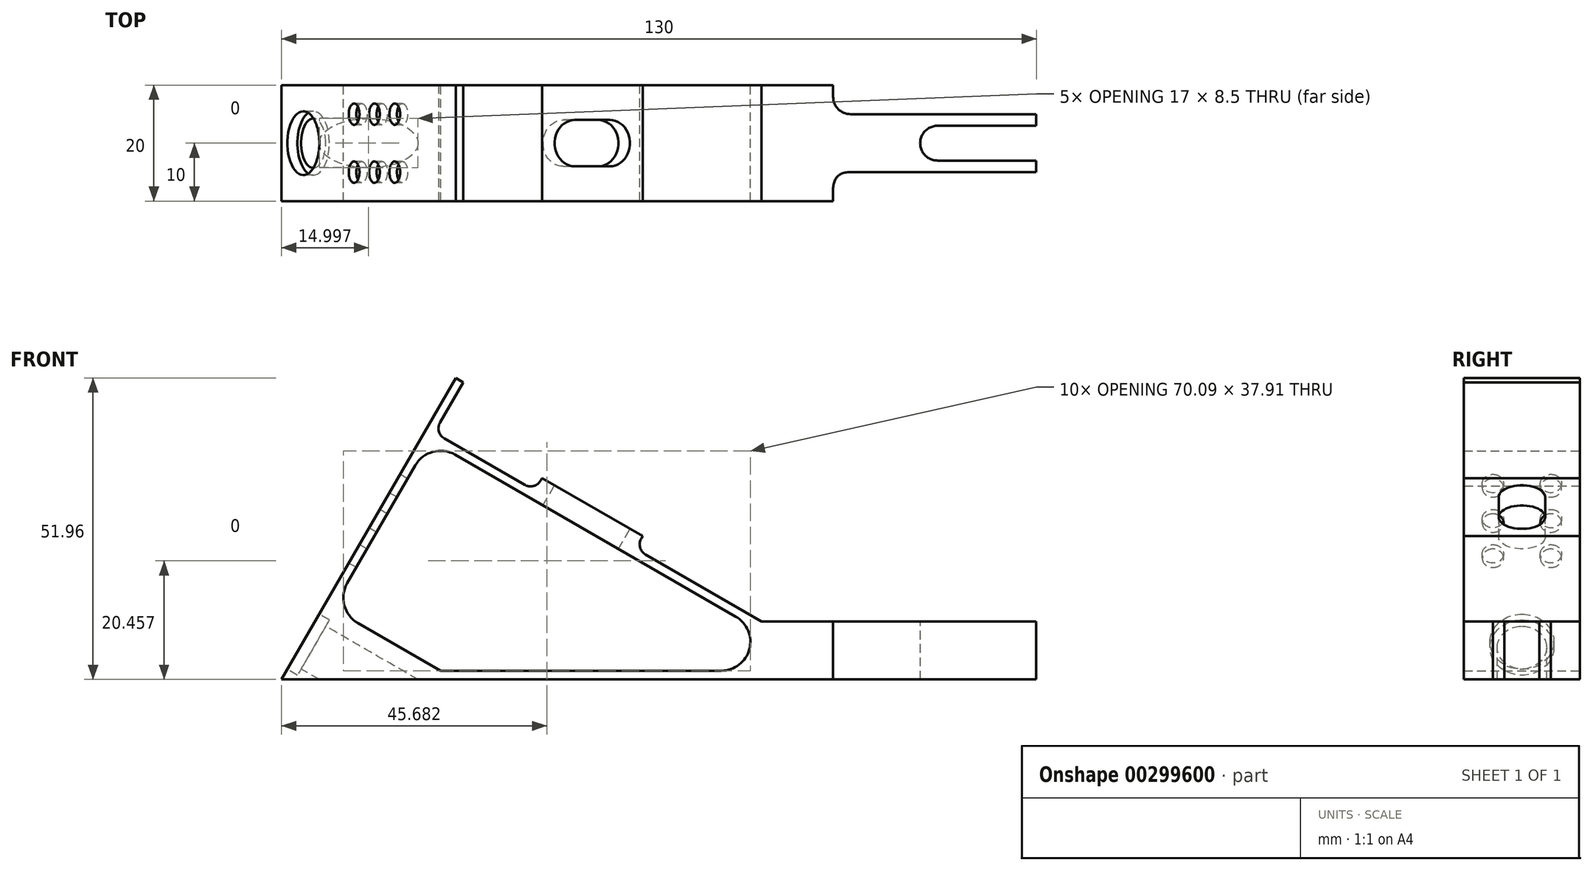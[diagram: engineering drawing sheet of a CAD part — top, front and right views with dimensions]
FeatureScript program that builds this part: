
annotation { "Feature Type Name" : "Feature", "Feature Type Description" : "" }
export const myFeature = defineFeature(function(context is Context, id is Id, definition is map)
    precondition{}
    {
        {
            var Q0;
            Q0=qCreatedBy(makeId("Front.planeOp"),FACE);
            var sketch = newSketch(context, id + "F0", { "sketchPlane" : qUnion([Q0])});
            skLineSegment(sketch, "E0", {"start": v(47.67, 58.9) * mm, "end": v(48.97, 58.14) * mm});
            skLineSegment(sketch, "E1", {"start": v(48.97, 58.14) * mm, "end": v(43.97, 49.48) * mm});
            skLineSegment(sketch, "E2", {"start": v(43.97, 49.48) * mm, "end": v(48.97, 46.6) * mm});
            skLineSegment(sketch, "E3", {"start": v(78.6, 29.48) * mm, "end": v(100.35, 16.93) * mm});
            skLineSegment(sketch, "E4", {"start": v(100.35, 16.93) * mm, "end": v(147.67, 16.93) * mm});
            skLineSegment(sketch, "E5", {"start": v(147.67, 16.93) * mm, "end": v(147.67, 6.93) * mm});
            skLineSegment(sketch, "E6", {"start": v(147.67, 6.93) * mm, "end": v(17.67, 6.93) * mm});
            skLineSegment(sketch, "E7", {"start": v(47.67, 58.9) * mm, "end": v(17.67, 6.93) * mm});
            skLineSegment(sketch, "E8", {"start": v(30.8, 16.67) * mm, "end": v(45.07, 8.43) * mm});
            skLineSegment(sketch, "E9", {"start": v(45.07, 8.43) * mm, "end": v(93.4, 8.43) * mm});
            skArc(sketch, "E10", {"start": v(93.4, 8.43) * mm, "mid": v(98.24, 12.14) * mm, "end": v(95.9, 17.76) * mm});
            skLineSegment(sketch, "E11", {"start": v(95.9, 17.76) * mm, "end": v(47.55, 45.68) * mm});
            skArc(sketch, "E12", {"start": v(47.55, 45.68) * mm, "mid": v(43.75, 46.18) * mm, "end": v(40.72, 43.85) * mm});
            skLineSegment(sketch, "E13", {"start": v(40.72, 43.85) * mm, "end": v(28.97, 23.5) * mm});
            skArc(sketch, "E14", {"start": v(28.97, 23.5) * mm, "mid": v(28.47, 19.7) * mm, "end": v(30.8, 16.67) * mm});
            skPoint(sketch, "E15.start.orphan", {"position": v(50.22, 48.76) * mm});
            skPoint(sketch, "E16.start.orphan", {"position": v(67.54, 38.76) * mm});
            skLineSegment(sketch, "E17", {"start": v(48.97, 46.6) * mm, "end": v(61.29, 39.48) * mm});
            skLineSegment(sketch, "E18", {"start": v(61.29, 39.48) * mm, "end": v(62.54, 41.65) * mm});
            skLineSegment(sketch, "E19", {"start": v(62.54, 41.65) * mm, "end": v(79.86, 31.65) * mm});
            skLineSegment(sketch, "E20", {"start": v(79.86, 31.65) * mm, "end": v(78.6, 29.48) * mm});
            skPoint(sketch, "E21.orphan", {"position": v(66.29, 36.6) * mm});
            skSolve(sketch);
        }
        {
            var Q0;
            Q0 = qSketchRegion(id + "F0", true);
            extrude(context, id + "F1", {"entities" : qUnion([Q0]), "depth" : 20 * mm});
        }
        {
            var Q0;
            Q0=makeQuery(id+"F1.opExtrude","CAP_FACE",FACE,{"disambiguationData":[OSD([sQuery(id+"F0.wireOp",EDGE,"E0"),sQuery(id+"F0.wireOp",EDGE,"E1"),sQuery(id+"F0.wireOp",EDGE,"E2"),sQuery(id+"F0.wireOp",EDGE,"u1qnqnEZ-ZZXt-tcXC-5rbI-ApPhX4VsB7uH"),sQuery(id+"F0.wireOp",EDGE,"E15"),sQuery(id+"F0.wireOp",EDGE,"E16"),sQuery(id+"F0.wireOp",EDGE,"E3"),sQuery(id+"F0.wireOp",EDGE,"E4"),sQuery(id+"F0.wireOp",EDGE,"E5"),sQuery(id+"F0.wireOp",EDGE,"E6"),sQuery(id+"F0.wireOp",EDGE,"E7"),sQuery(id+"F0.wireOp",EDGE,"E8"),sQuery(id+"F0.wireOp",EDGE,"E9"),sQuery(id+"F0.wireOp",EDGE,"E10"),sQuery(id+"F0.wireOp",EDGE,"E11"),sQuery(id+"F0.wireOp",EDGE,"E12"),sQuery(id+"F0.wireOp",EDGE,"E13"),sQuery(id+"F0.wireOp",EDGE,"E14")])],"isStart":false});
            var sketch = newSketch(context, id + "F2", { "sketchPlane" : qUnion([Q0])});
            skLineSegment(sketch, "E22", {"start": v(112.67, 16.93) * mm, "end": v(112.67, 6.93) * mm});
            skSolve(sketch);
        }
        {
            var Q0;
            Q0 = qSketchRegion(id + "F2", true);
            var Q1;
            {var subQ0=sQuery(id+"F2.wireOp",EDGE,"E22");Q1=makeQuery(id+"F2.imprint","IMPRINT",FACE,{"disambiguationData":[TD([[makeQuery(id+"F2.imprint","IMPRINT",EDGE,{"derivedFrom":subQ0}),1.0]])]});}
            extrude(context, id + "F3", {"entities" : qUnion([Q0, Q1]), "operationType" : NewBodyOperationType.REMOVE, "oppositeDirection" : true, "depth" : 5 * mm});
        }
        {
            var Q0;
            Q0=makeQuery(id+"F1.opExtrude","CAP_FACE",FACE,{"disambiguationData":[OSD([sQuery(id+"F0.wireOp",EDGE,"E0"),sQuery(id+"F0.wireOp",EDGE,"E1"),sQuery(id+"F0.wireOp",EDGE,"E2"),sQuery(id+"F0.wireOp",EDGE,"u1qnqnEZ-ZZXt-tcXC-5rbI-ApPhX4VsB7uH"),sQuery(id+"F0.wireOp",EDGE,"E15"),sQuery(id+"F0.wireOp",EDGE,"E16"),sQuery(id+"F0.wireOp",EDGE,"E3"),sQuery(id+"F0.wireOp",EDGE,"E4"),sQuery(id+"F0.wireOp",EDGE,"E5"),sQuery(id+"F0.wireOp",EDGE,"E6"),sQuery(id+"F0.wireOp",EDGE,"E7"),sQuery(id+"F0.wireOp",EDGE,"E8"),sQuery(id+"F0.wireOp",EDGE,"E9"),sQuery(id+"F0.wireOp",EDGE,"E10"),sQuery(id+"F0.wireOp",EDGE,"E11"),sQuery(id+"F0.wireOp",EDGE,"E12"),sQuery(id+"F0.wireOp",EDGE,"E13"),sQuery(id+"F0.wireOp",EDGE,"E14")])],"isStart":true});
            var sketch = newSketch(context, id + "F4", { "sketchPlane" : qUnion([Q0])});
            skLineSegment(sketch, "E23", {"start": v(-112.67, 16.93) * mm, "end": v(-112.67, 6.93) * mm});
            skSolve(sketch);
        }
        {
            var Q0;
            Q0 = qSketchRegion(id + "F4", true);
            var Q1;
            {var subQ0=sQuery(id+"F4.wireOp",EDGE,"E23");Q1=makeQuery(id+"F4.imprint","IMPRINT",FACE,{"disambiguationData":[TD([[makeQuery(id+"F4.imprint","IMPRINT",EDGE,{"derivedFrom":subQ0}),-1.0]])]});}
            extrude(context, id + "F5", {"entities" : qUnion([Q0, Q1]), "operationType" : NewBodyOperationType.REMOVE, "oppositeDirection" : true, "depth" : 5 * mm});
        }
        {
            var Q0;
            Q0=makeQuery(id+"F1.opExtrude","SWEPT_FACE",FACE,{"disambiguationData":[OSD([sQuery(id+"F0.wireOp",EDGE,"E4")])]});
            var sketch = newSketch(context, id + "F6", { "sketchPlane" : qUnion([Q0])});
            skArc(sketch, "E24", {"start": v(130.67, -7) * mm, "mid": v(127.67, -10) * mm, "end": v(130.67, -13) * mm});
            skLineSegment(sketch, "E25", {"start": v(130.66, -7) * mm, "end": v(147.67, -7) * mm});
            skLineSegment(sketch, "E26", {"start": v(130.67, -13) * mm, "end": v(147.67, -13) * mm});
            skSolve(sketch);
        }
        {
            var Q0;
            Q0 = qSketchRegion(id + "F6", true);
            var Q1;
            {var subQ5=sQuery(id+"F6.wireOp",EDGE,"E24");Q1=makeQuery(id+"F6.imprint","IMPRINT",FACE,{"disambiguationData":[TD([[makeQuery(id+"F6.imprint","IMPRINT",EDGE,{"derivedFrom":subQ5}),1.0]])]});}
            extrude(context, id + "F7", {"entities" : qUnion([Q0, Q1]), "operationType" : NewBodyOperationType.REMOVE, "oppositeDirection" : true, "depth" : 25 * mm});
        }
        {
            var Q0;
            Q0=makeQuery(id+"F3.boolean.opBoolean","COPY",EDGE,{"derivedFrom":makeQuery(id+"F3.opExtrude","CAP_EDGE",EDGE,{"disambiguationData":[OSD([sQuery(id+"F2.wireOp",EDGE,"E22")])],"isStart":false})});
            fillet(context, id + "F8", {"entities" : qUnion([Q0]), "radius" : 3 * mm, "tangentPropagation" : true, "rho" : 0.5, "crossSection" : FilletCrossSection.CONIC, "allowEdgeOverflow" : false});
        }
        {
            var Q0;
            Q0=makeQuery(id+"F5.boolean.opBoolean","COPY",EDGE,{"derivedFrom":makeQuery(id+"F5.opExtrude","CAP_EDGE",EDGE,{"disambiguationData":[OSD([sQuery(id+"F4.wireOp",EDGE,"E23")])],"isStart":false})});
            fillet(context, id + "F9", {"entities" : qUnion([Q0]), "radius" : 3 * mm, "tangentPropagation" : true, "allowEdgeOverflow" : false});
        }
        {
            var Q0;
            Q0=makeQuery(id+"F1.opExtrude","SWEPT_EDGE",EDGE,{"disambiguationData":[OSD([sQuery(id+"F0.wireOp",EDGE,"E3"),sQuery(id+"F0.wireOp",EDGE,"E20")])]});
            fillet(context, id + "F10", {"entities" : qUnion([Q0]), "radius" : 2 * mm, "tangentPropagation" : true, "allowEdgeOverflow" : false});
        }
        {
            var Q0;
            Q0=makeQuery(id+"F1.opExtrude","SWEPT_EDGE",EDGE,{"disambiguationData":[OSD([sQuery(id+"F0.wireOp",EDGE,"E17"),sQuery(id+"F0.wireOp",EDGE,"E18")])]});
            fillet(context, id + "F11", {"entities" : qUnion([Q0]), "radius" : 2 * mm, "tangentPropagation" : true, "allowEdgeOverflow" : false});
        }
        {
            var Q0;
            Q0=makeQuery(id+"F1.opExtrude","SWEPT_EDGE",EDGE,{"disambiguationData":[OSD([sQuery(id+"F0.wireOp",EDGE,"E1"),sQuery(id+"F0.wireOp",EDGE,"E2")])]});
            fillet(context, id + "F12", {"entities" : qUnion([Q0]), "radius" : 2 * mm, "tangentPropagation" : true, "allowEdgeOverflow" : false});
        }
        {
            var Q0;
            Q0=makeQuery(id+"F1.opExtrude","SWEPT_FACE",FACE,{"disambiguationData":[OSD([sQuery(id+"F0.wireOp",EDGE,"E19")])]});
            var sketch = newSketch(context, id + "F13", { "sketchPlane" : qUnion([Q0])});
            skLineSegment(sketch, "E27", {"start": v(39.83, -10) * mm, "end": v(46.83, -10) * mm, "construction": true});
            skPoint(sketch, "E27.startSnap0", {"position": v(33.33, -10) * mm});
            skArc(sketch, "E28", {"start": v(39.83, -6) * mm, "mid": v(35.83, -10) * mm, "end": v(39.83, -14) * mm});
            skArc(sketch, "E29", {"start": v(46.83, -6) * mm, "mid": v(50.83, -10) * mm, "end": v(46.83, -14) * mm});
            skLineSegment(sketch, "E30", {"start": v(39.83, -6) * mm, "end": v(46.83, -6) * mm});
            skLineSegment(sketch, "E31", {"start": v(46.83, -14) * mm, "end": v(39.83, -14) * mm});
            skSolve(sketch);
        }
        {
            var Q0;
            Q0 = qSketchRegion(id + "F13", true);
            extrude(context, id + "F14", {"entities" : qUnion([Q0]), "operationType" : NewBodyOperationType.REMOVE, "oppositeDirection" : true, "depth" : 15 * mm});
        }
        {
            var Q0;
            Q0=makeQuery(id+"F1.opExtrude","SWEPT_FACE",FACE,{"disambiguationData":[OSD([sQuery(id+"F0.wireOp",EDGE,"E7")])]});
            var sketch = newSketch(context, id + "F15", { "sketchPlane" : qUnion([Q0])});
            skCircle(sketch, "E32", {"center": v(10, 22.34) * mm, "radius": 5.5 * mm});
            skSolve(sketch);
        }
        {
            var Q0;
            Q0 = qSketchRegion(id + "F15", true);
            extrude(context, id + "F16", {"entities" : qUnion([Q0]), "operationType" : NewBodyOperationType.REMOVE, "oppositeDirection" : true, "depth" : 2 * mm});
        }
        {
            var Q0;
            Q0=makeQuery(id+"F16.boolean.opBoolean","COPY",FACE,{"derivedFrom":makeQuery(id+"F16.opExtrude","CAP_FACE",FACE,{"disambiguationData":[OSD([sQuery(id+"F15.wireOp",EDGE,"E32")])],"isStart":false})});
            var sketch = newSketch(context, id + "F17", { "sketchPlane" : qUnion([Q0])});
            skCircle(sketch, "E33", {"center": v(10, 22.34) * mm, "radius": 4.25 * mm});
            skSolve(sketch);
        }
        {
            var Q0;
            Q0 = qSketchRegion(id + "F17", true);
            extrude(context, id + "F18", {"entities" : qUnion([Q0]), "operationType" : NewBodyOperationType.REMOVE, "endBound" : BoundingType.THROUGH_ALL, "oppositeDirection" : true, "depth" : 25 * mm});
        }
        {
            var Q0;
            Q0=makeQuery(id+"F1.opExtrude","SWEPT_FACE",FACE,{"disambiguationData":[OSD([sQuery(id+"F0.wireOp",EDGE,"E7")])]});
            var sketch = newSketch(context, id + "F19", { "sketchPlane" : qUnion([Q0])});
            skCircle(sketch, "E34", {"center": v(15, 53.84) * mm, "radius": 1.84 * mm});
            skCircle(sketch, "E35", {"center": v(5, 53.84) * mm, "radius": 1.84 * mm});
            skCircle(sketch, "E36", {"center": v(5, 46.84) * mm, "radius": 1.84 * mm});
            skCircle(sketch, "E37", {"center": v(15, 46.84) * mm, "radius": 1.84 * mm});
            skCircle(sketch, "E38", {"center": v(15, 39.84) * mm, "radius": 1.84 * mm});
            skCircle(sketch, "E39", {"center": v(5, 39.84) * mm, "radius": 1.84 * mm});
            skSolve(sketch);
        }
        {
            var Q0;
            Q0 = qSketchRegion(id + "F19", true);
            extrude(context, id + "F20", {"entities" : qUnion([Q0]), "operationType" : NewBodyOperationType.REMOVE, "oppositeDirection" : true, "depth" : 10 * mm});
        }
    });
